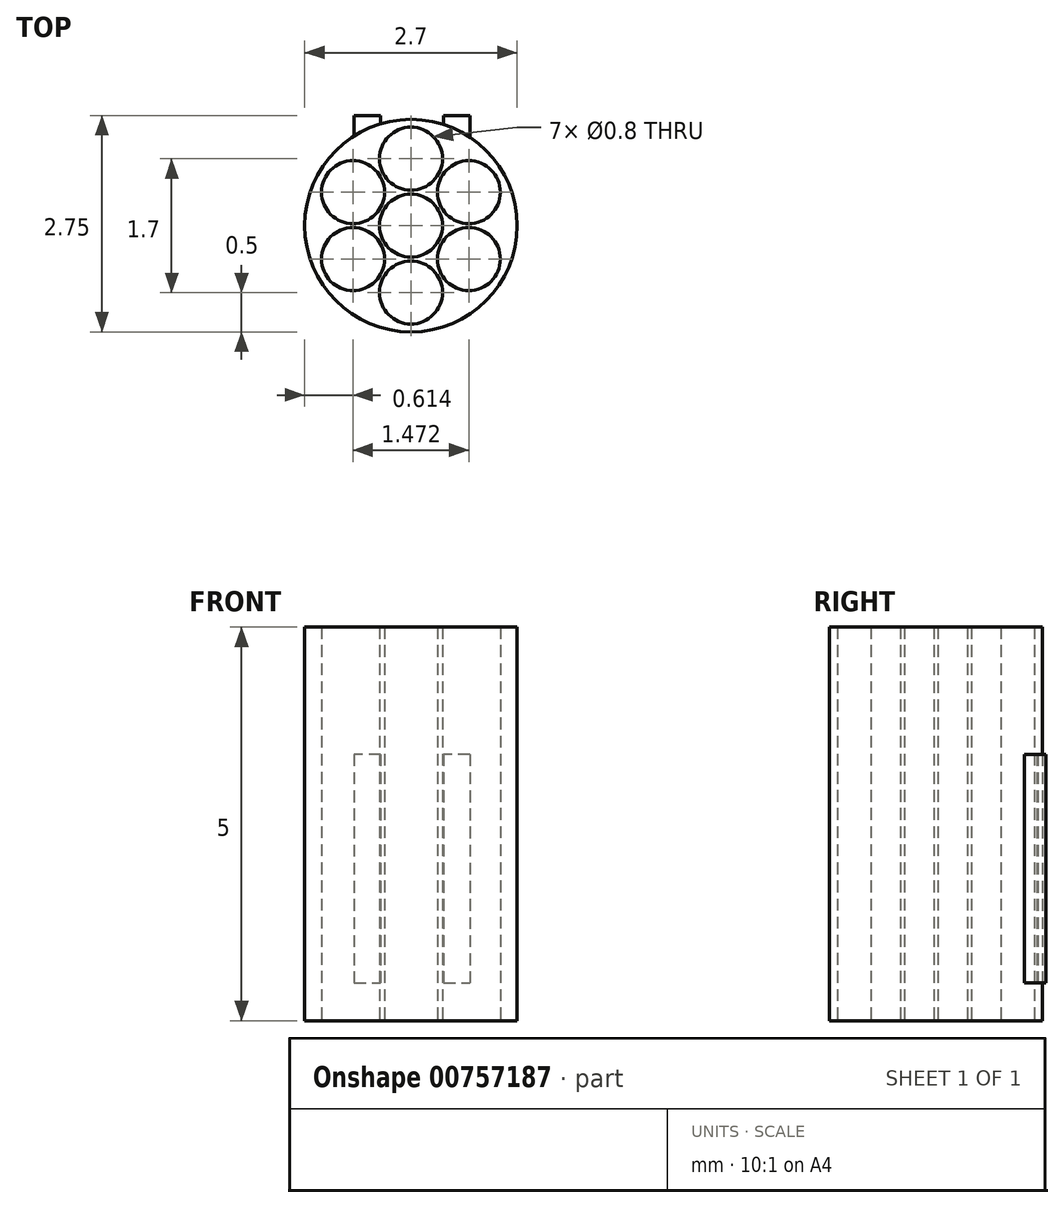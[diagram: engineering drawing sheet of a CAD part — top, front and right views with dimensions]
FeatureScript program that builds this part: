
annotation { "Feature Type Name" : "Feature", "Feature Type Description" : "" }
export const myFeature = defineFeature(function(context is Context, id is Id, definition is map)
    precondition{}
    {
        {
            var Q0;
            Q0=qCreatedBy(makeId("Top.planeOp"),FACE);
            var sketch = newSketch(context, id + "F0", { "sketchPlane" : qUnion([Q0])});
            skCircle(sketch, "E0", {"center": v(0, 0) * mm, "radius": 0.85 * mm});
            skCircle(sketch, "E1.cCircle", {"center": v(0, 0) * mm, "radius": 0.85 * mm, "construction": true});
            skLineSegment(sketch, "E1.0", {"start": v(0, 0.85) * mm, "end": v(0.74, 0.43) * mm});
            skLineSegment(sketch, "E1.1", {"start": v(0.74, 0.43) * mm, "end": v(0.74, -0.43) * mm});
            skLineSegment(sketch, "E1.2", {"start": v(0.74, -0.43) * mm, "end": v(0, -0.85) * mm});
            skLineSegment(sketch, "E1.3", {"start": v(0, -0.85) * mm, "end": v(-0.74, -0.43) * mm});
            skLineSegment(sketch, "E1.4", {"start": v(-0.74, -0.43) * mm, "end": v(-0.74, 0.42) * mm});
            skLineSegment(sketch, "E1.5", {"start": v(-0.74, 0.42) * mm, "end": v(0, 0.85) * mm});
            skSolve(sketch);
        }
        {
            var Q0;
            Q0=qCreatedBy(makeId("Top.planeOp"),FACE);
            var sketch = newSketch(context, id + "F1", { "sketchPlane" : qUnion([Q0])});
            skCircle(sketch, "E2", {"center": v(0, 0) * mm, "radius": 0.4 * mm});
            skCircle(sketch, "E3", {"center": v(0, 0.85) * mm, "radius": 0.4 * mm});
            skCircle(sketch, "E4", {"center": v(0.74, 0.43) * mm, "radius": 0.4 * mm});
            skCircle(sketch, "E5", {"center": v(0.74, -0.43) * mm, "radius": 0.4 * mm});
            skCircle(sketch, "E6", {"center": v(0, -0.85) * mm, "radius": 0.4 * mm});
            skCircle(sketch, "E7", {"center": v(-0.74, -0.43) * mm, "radius": 0.4 * mm});
            skCircle(sketch, "E8", {"center": v(-0.74, 0.42) * mm, "radius": 0.4 * mm});
            skSolve(sketch);
        }
        {
            var Q0;
            Q0=qCreatedBy(makeId("Top.planeOp"),FACE);
            var sketch = newSketch(context, id + "F2", { "sketchPlane" : qUnion([Q0])});
            skCircle(sketch, "E9", {"center": v(0, 0) * mm, "radius": 1.35 * mm});
            skSolve(sketch);
        }
        {
            var Q0;
            Q0=qSketchRegion(id+"F2",true);
            extrude(context, id + "F3", {"entities" : qUnion([Q0]), "depth" : 5 * mm, "offsetDistance" : 25 * mm});
        }
        {
            var Q0;
            Q0=qSketchRegion(id+"F1",true);
            extrude(context, id + "F4", {"entities" : qUnion([Q0]), "operationType" : NewBodyOperationType.REMOVE, "endBound" : BoundingType.THROUGH_ALL, "depth" : 25 * mm, "offsetDistance" : 25 * mm});
        }
        {
            var Q0;
            Q0=makeQuery(id+"F3.opExtrude","CAP_FACE",FACE,{"disambiguationData":[OSD([sQuery(id+"F2.wireOp",EDGE,"E9")])],"isStart":false});
            var sketch = newSketch(context, id + "F5", { "sketchPlane" : qUnion([Q0])});
            skPoint(sketch, "E10", {"position": v(0, -1.35) * mm});
            skPoint(sketch, "E11", {"position": v(-0.36, -1.35) * mm});
            skPoint(sketch, "E12", {"position": v(0.42, -1.35) * mm});
            skSolve(sketch);
        }
        {
            var Q0;
            Q0=makeQuery(id+"F3.opExtrude","CAP_FACE",FACE,{"disambiguationData":[OSD([sQuery(id+"F2.wireOp",EDGE,"E9")])],"isStart":true});
            var sketch = newSketch(context, id + "F6", { "sketchPlane" : qUnion([Q0])});
            skPoint(sketch, "E13", {"position": v(0, 1.35) * mm});
            skPoint(sketch, "E14", {"position": v(-0.36, 1.35) * mm});
            skPoint(sketch, "E15", {"position": v(0.42, 1.35) * mm});
            skSolve(sketch);
        }
        {
            var Q0;
            Q0=sQuery(id+"F5.wireOp",VERTEX,"E10");
            var Q1;
            Q1=sQuery(id+"F6.wireOp",VERTEX,"E13");
            var Q2;
            Q2=sQuery(id+"F6.wireOp",VERTEX,"E15");
            cPlane(context, id + "F7", {"entities" : qUnion([Q0, Q1, Q2]), "cplaneType" : CPlaneType.THREE_POINT, "offset" : 0 * mm, "oppositeDirection" : true, "width" : 150 * mm, "height" : 150 * mm});
        }
        {
            var Q0;
            Q0=qCreatedBy(id+"F7.planeOp",FACE);
            cPlane(context, id + "F8", {"entities" : qUnion([Q0]), "cplaneType" : CPlaneType.OFFSET, "offset" : 2.4 * mm, "width" : 150 * mm, "height" : 150 * mm});
        }
        {
            var Q0;
            Q0=qCreatedBy(id+"F8.planeOp",FACE);
            var sketch = newSketch(context, id + "F9", { "sketchPlane" : qUnion([Q0])});
            skText(sketch, "E16", { "text": "II", "fontName": "OpenSans-Regular.ttf"});
            const initialGuessF9  = {"E16": [-0.00115, 0.00048, 1, 0, 0.00293]};
            skSetInitialGuess(sketch, initialGuessF9);
            skSolve(sketch);
        }
        {
            var Q0;
            Q0=qSketchRegion(id+"F9",true);
            extrude(context, id + "F10", {"entities" : qUnion([Q0]), "operationType" : NewBodyOperationType.ADD, "depth" : 0.35 * mm, "offsetDistance" : 25 * mm});
        }
    });
